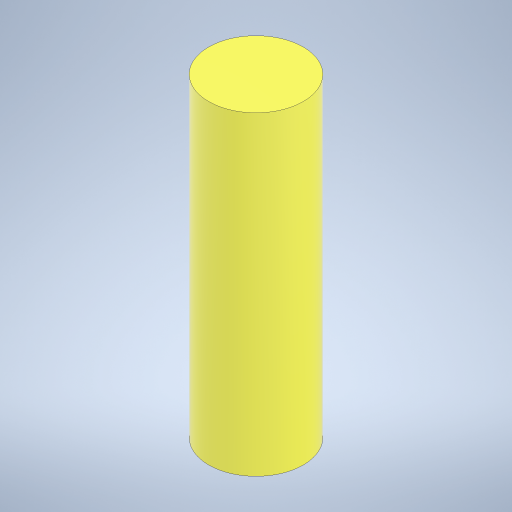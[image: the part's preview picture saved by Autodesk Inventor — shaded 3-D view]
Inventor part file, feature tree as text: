
AUTODESK INVENTOR PART (.ipt)
format: ipt  version: 2024.3 (Build 283343000, 343)  size: 217,600 bytes
history: native  units: mm
features: extrude x1, sketch x1
ambient origin geometry x8: Origin, YZ Plane, XZ Plane, XY Plane, X Axis, Y Axis, Z Axis, Center Point
bodies: Solid1 (feature_tree)
feature tree (2):
  extrude  "Extrusion1"  Depth=10.0mm TaperAngle=0.0deg
  sketch  "Sketch1"  dims[d0=3.0mm d1=10.0mm d2=0.0mm]
